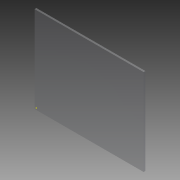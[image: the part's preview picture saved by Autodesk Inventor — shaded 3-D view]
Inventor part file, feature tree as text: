
AUTODESK INVENTOR PART (.ipt)
format: ipt  version: 2015 (Build 190159000, 159)  size: 83,968 bytes
history: native  units: in
note: dims shown in document units (in); Inventor stores cm internally (conversion verified against a paired STEP export)
features: sketch x2, extrude x1
ambient origin geometry x8: Origin, YZ Plane, XZ Plane, XY Plane, X Axis, Y Axis, Z Axis, Center Point
bodies: Solid1 (feature_tree)
feature tree (3):
  sketch  "Sketch1"  dims[d0=16.1417in d1=12.7953in]
  extrude  "Extrusion1"  Depth=12.7953in
  sketch  "Sketch2"  dims[d2=0.2756in d3=0.0in]
